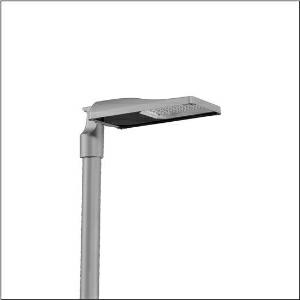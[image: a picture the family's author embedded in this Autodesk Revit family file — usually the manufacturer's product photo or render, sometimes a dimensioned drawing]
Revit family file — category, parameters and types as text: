
# Revit family: streetlight_sl_31_mini___st1_0a_5xh2d3aa08ja_eb00
name_source: partatom
category: Lighting Fixtures
units: mm (PartAtom-declared; Revit-internal decimal feet)

## family parameters
Cut with Voids When Loaded = No
Host = Face
Light Source = No
Part Type = Normal
Room Calculation Point = No
Round Connector Dimension = Use Diameter
Shared = No

## types (1)
- --- (1 x LED, 12140 lm, 81.1 W, 3000K)
    Apparent Load = 81 VA
    CIE Flux Codes = 40 73 97 100 100
    Color Rendering = 70
    Color Temperature = 3000K
    Default Elevation = 1800 mm
    Description = Streetlight SL 31 mini Easy mast luminaire for post-top, side-entry; light control with lens of PMMA; light distribution: ST1.0a, direct asymmetric distribution, for standard-compliant lighting for roads and squares; LED: luminous flux: 12.140lm, light colour: 730, colour temperature: 3000K; luminous efficacy: 149,7lm/W; control: overheat protection, intelligent temperature release in ECG and LED module, constant luminous flux control, time-dependent luminous flux control, flexible luminous flux parameterisation, pre-setting: linear dimming characteristic; luminaire housing, of diecast aluminium, SITECO metallic grey (DB 702S), corrosivity category C5 high according to DIN EN ISO 12944; cover of toughened safety glass, transparent, mast flange of diecast aluminium, SITECO metallic grey (DB 702S), spigot size: 76/60mm, mast flange included unmounted; cable length: 10,5m, connection cable pre-assembled; mains connection: 220..240V, AC, 50/60Hz; power consumption (at start of service life): 81,1W / (at end of service life): 88,3W / (with reduced operation 50%): 36,4W; protection rating (complete): IP66; insulation class (complete): insulation class II (safety insulation); impact resistance: IK10; certification: CE, ENEC, ENEC+, VDE, UKCA; permissible operating ambient temperature for outdoor applications: -40..+50°C; packaging unit: 1 piece

Light Distribution: ST1.0a
    Height = 76 mm
    Lamp = 1 x LED
    Lamp Light Flux = 12140 lm
    Lamp Power = 81.1 W
    Lamp count = 1
    Length = 547 mm
    Luminous efficacy = 150 lm/W
    Manufacturer = Siteco
    ModVariant = No
    Model = 5XH2D3AA08JA
    Number of Poles = 1
    OnlyDefault = Yes
    Power Factor = 1
    Product Name = Streetlight SL 31 mini | ST1.0a
    Product group = mast luminaire | pylon top
    ProductGroupID = 6100
    Protection Class = Protection class II
    Protection Degree = IP 66
    RLX_Detail_Level = 1
    RLX_Emergency_Light_Flux = 0 lm
    RLX_Emergency_Type = 0
    RLX_Emergency_Type_DB = No
    RlxData = <blob elided: 39753 chars, md5=e7ceddc0>
    Socket = socket
    Standby Power = 0 W
    System Light Flux = 12140 lm
    System Power = 81 W
    Type Comments = factory setting: luminous flux: 100 % | dim-lin: 254 | 860 mA
    Type Image = l_1300326.jpg
    URL = http://relux.com
    VarID = @adj_057915
    Voltage = 0 V
    Weight = 0.00 kg
    Width = 265 mm

## geometry (parser evidence)
native form markers: Blend x4, Sweep x10
no freeform markers — native parametric forms only
